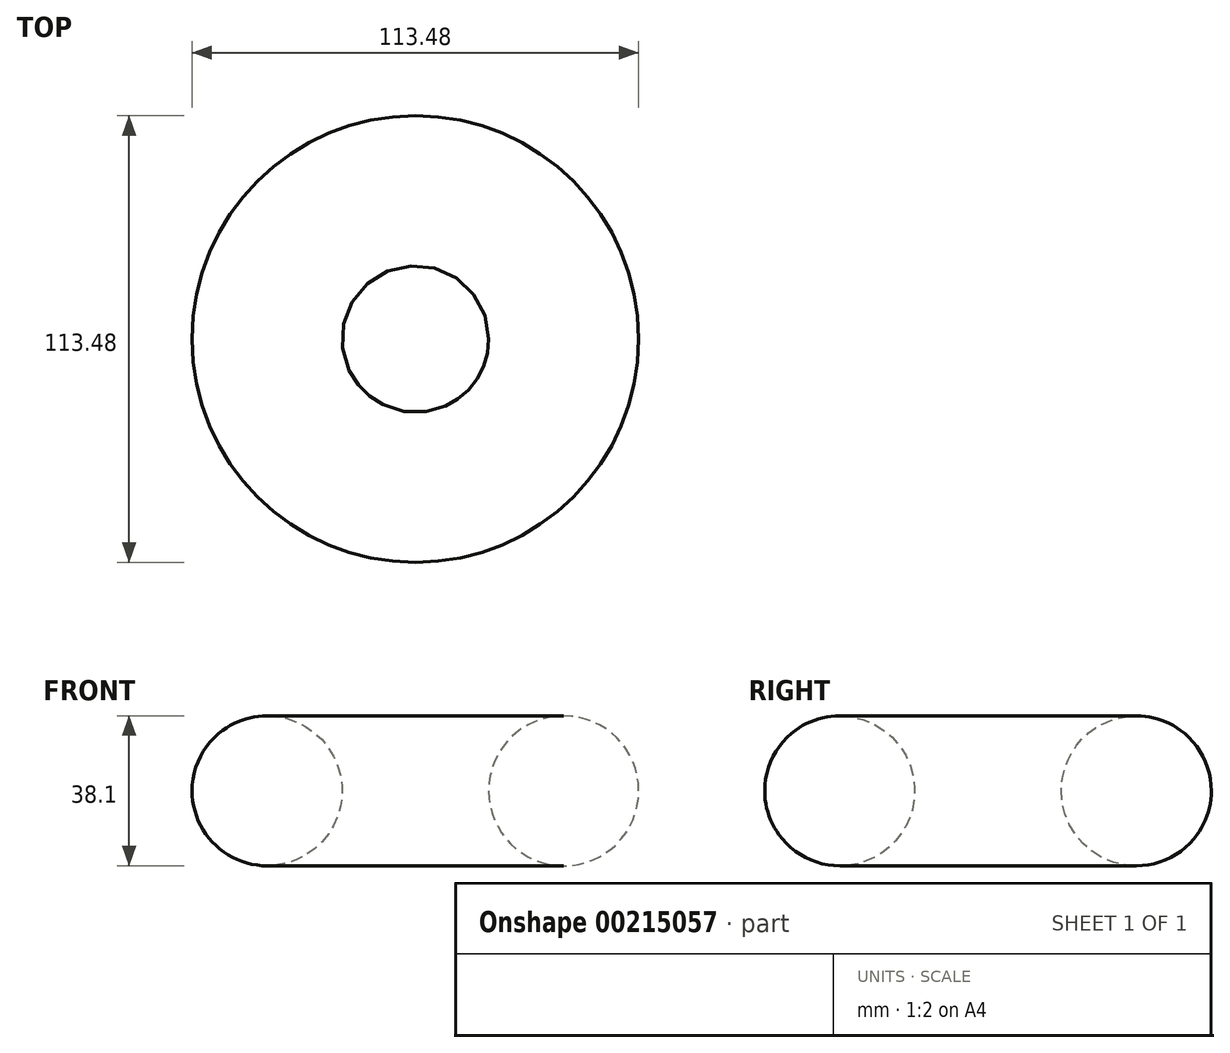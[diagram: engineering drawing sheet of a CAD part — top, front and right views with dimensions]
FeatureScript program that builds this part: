
annotation { "Feature Type Name" : "Feature", "Feature Type Description" : "" }
export const myFeature = defineFeature(function(context is Context, id is Id, definition is map)
    precondition{}
    {
        {
            var Q0;
            Q0=qCreatedBy(makeId("Front.planeOp"),FACE);
            var sketch = newSketch(context, id + "F0", { "sketchPlane" : qUnion([Q0])});
            skCircle(sketch, "E0", {"center": v(37.69, 0) * mm, "radius": 19.05 * mm});
            skSolve(sketch);
        }
        {
            var Q0;
            Q0=qCreatedBy(makeId("Front.planeOp"),FACE);
            var sketch = newSketch(context, id + "F1", { "sketchPlane" : qUnion([Q0])});
            skLineSegment(sketch, "E1", {"start": v(0, 34.2) * mm, "end": v(0, -28.77) * mm});
            skSolve(sketch);
        }
        {
            var Q0;
            Q0 = qSketchRegion(id + "F0", true);
            var Q1;
            Q1=sQuery(id+"F1.wireOp",EDGE,"E1");
            revolve(context, id + "F2", {"entities" : qUnion([Q0]), "axis" : qUnion([Q1]), "revolveType" : RevolveType.FULL});
        }
    });
